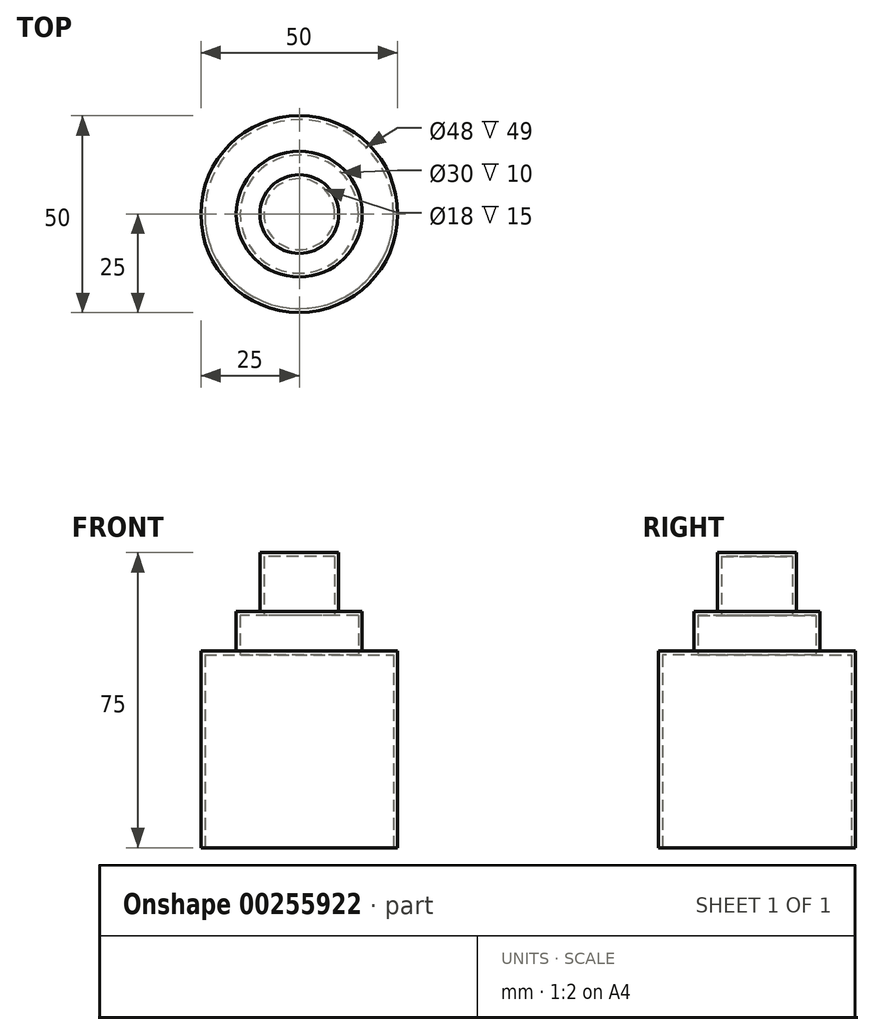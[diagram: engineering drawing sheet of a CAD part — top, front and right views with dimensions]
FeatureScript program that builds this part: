
annotation { "Feature Type Name" : "Feature", "Feature Type Description" : "" }
export const myFeature = defineFeature(function(context is Context, id is Id, definition is map)
    precondition{}
    {
        {
            var Q0;
            Q0=qCreatedBy(makeId("Front.planeOp"),FACE);
            var sketch = newSketch(context, id + "F0", { "sketchPlane" : qUnion([Q0])});
            skLineSegment(sketch, "E0", {"start": v(0, 0) * mm, "end": v(0, 75) * mm});
            skLineSegment(sketch, "E1", {"start": v(0, 0) * mm, "end": v(25, 0) * mm});
            skLineSegment(sketch, "E2", {"start": v(25, 0) * mm, "end": v(25, 50) * mm});
            skLineSegment(sketch, "E3", {"start": v(25, 50) * mm, "end": v(16, 50) * mm});
            skLineSegment(sketch, "E4", {"start": v(16, 50) * mm, "end": v(16, 60) * mm});
            skLineSegment(sketch, "E5", {"start": v(16, 60) * mm, "end": v(10, 60) * mm});
            skLineSegment(sketch, "E6", {"start": v(10, 60) * mm, "end": v(10, 75) * mm});
            skLineSegment(sketch, "E7", {"start": v(10, 75) * mm, "end": v(0, 75) * mm});
            skSolve(sketch);
        }
        {
            var Q0;
            Q0=makeQuery(id+"F0.imprint","IMPRINT",FACE,{"disambiguationData":[TD([[makeQuery(id+"F0.imprint","IMPRINT",EDGE,{"derivedFrom":sQuery(id+"F0.wireOp",EDGE,"E0")}),-1.0]])]});
            var Q1;
            Q1=sQuery(id+"F0.wireOp",EDGE,"E0");
            revolve(context, id + "F1", {"entities" : qUnion([Q0]), "axis" : qUnion([Q1]), "revolveType" : RevolveType.FULL});
        }
        {
            var Q0;
            Q0=makeQuery(id+"F1.opRevolve","SWEPT_FACE",FACE,{"disambiguationData":[OSD([sQuery(id+"F0.wireOp",EDGE,"E1")])]});
            shell(context, id + "F2", {"entities" : qUnion([Q0]), "thickness" : 1 * mm});
        }
    });
